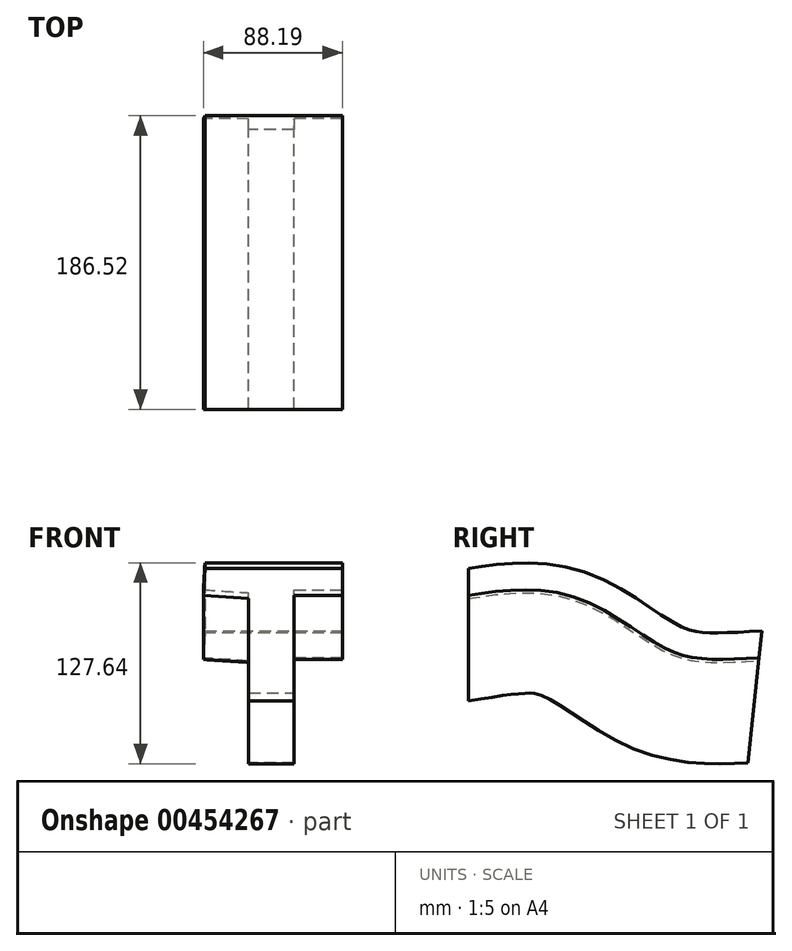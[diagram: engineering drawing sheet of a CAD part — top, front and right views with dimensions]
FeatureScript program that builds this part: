
annotation { "Feature Type Name" : "Feature", "Feature Type Description" : "" }
export const myFeature = defineFeature(function(context is Context, id is Id, definition is map)
    precondition{}
    {
        {
            var Q0;
            Q0=qCreatedBy(makeId("Front.planeOp"),FACE);
            var sketch = newSketch(context, id + "F0", { "sketchPlane" : qUnion([Q0])});
            skLineSegment(sketch, "E0", {"start": v(-45.06, 40.5) * mm, "end": v(42.18, 40.5) * mm});
            skLineSegment(sketch, "E1", {"start": v(42.18, 40.5) * mm, "end": v(42.18, 23.25) * mm});
            skLineSegment(sketch, "E2", {"start": v(42.18, 23.25) * mm, "end": v(11.5, 23.25) * mm});
            skLineSegment(sketch, "E3", {"start": v(11.5, 23.25) * mm, "end": v(11.5, -43.86) * mm});
            skLineSegment(sketch, "E4", {"start": v(11.5, -43.86) * mm, "end": v(-17.26, -43.86) * mm});
            skLineSegment(sketch, "E5", {"start": v(-17.26, -43.86) * mm, "end": v(-17.26, 21.33) * mm});
            skLineSegment(sketch, "E6", {"start": v(-17.26, 21.33) * mm, "end": v(-46.01, 23.25) * mm});
            skLineSegment(sketch, "E7", {"start": v(-46.01, 23.25) * mm, "end": v(-45.06, 40.5) * mm});
            skSolve(sketch);
        }
        {
            var Q0;
            Q0=qCreatedBy(makeId("Right.planeOp"),FACE);
            var sketch = newSketch(context, id + "F1", { "sketchPlane" : qUnion([Q0])});
            skFitSpline(sketch, "E8", {"points": [v(0, 0) * mm, v(61.2, 0) * mm, v(121.71, -33.94) * mm, v(182.3, -39.47) * mm], "startDerivative": vector(191.65, 30.72) * mm, "endDerivative": vector(190.08, 10.43) * mm});
            skSolve(sketch);
        }
        {
            var Q0;
            Q0=makeQuery(id+"F0.imprint","IMPRINT",FACE,{"disambiguationData":[TD([[makeQuery(id+"F0.imprint","IMPRINT",EDGE,{"derivedFrom":sQuery(id+"F0.wireOp",EDGE,"E0")}),-1.0]])]});
            var Q1;
            Q1=sQuery(id+"F1.wireOp",EDGE,"E8");
            sweep(context, id + "F2", {"profiles" : qUnion([Q0]), "path" : qUnion([Q1])});
        }
    });
